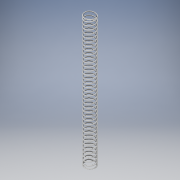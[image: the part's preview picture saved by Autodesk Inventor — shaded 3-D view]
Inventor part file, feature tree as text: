
AUTODESK INVENTOR PART (.ipt)
format: ipt  version: 2018 (Build 220112000, 112)  size: 835,072 bytes
history: native  units: in
note: dims shown in document units (in); Inventor stores cm internally (conversion verified against a paired STEP export)
features: helix x1, sketch x1
ambient origin geometry x8: Origin, YZ Plane, XZ Plane, XY Plane, X Axis, Y Axis, Z Axis, Center Point
bodies: Solid1 (feature_tree)
feature tree (2):
  helix  "Coil1"  [1 undecoded]
  sketch  "Sketch1"  dims[d1=0.47in d2=1.0in d3=10.7in d4=14.1732in d5=0.0in d6=90.0deg d7=1.3056in d8=90.0deg d9=1.3056in]
note: 1 required parameter value undecoded (feature->parameter linkage not recoverable at this tier; creation-order binding heuristic only, values carry confidence <= 0.55)
